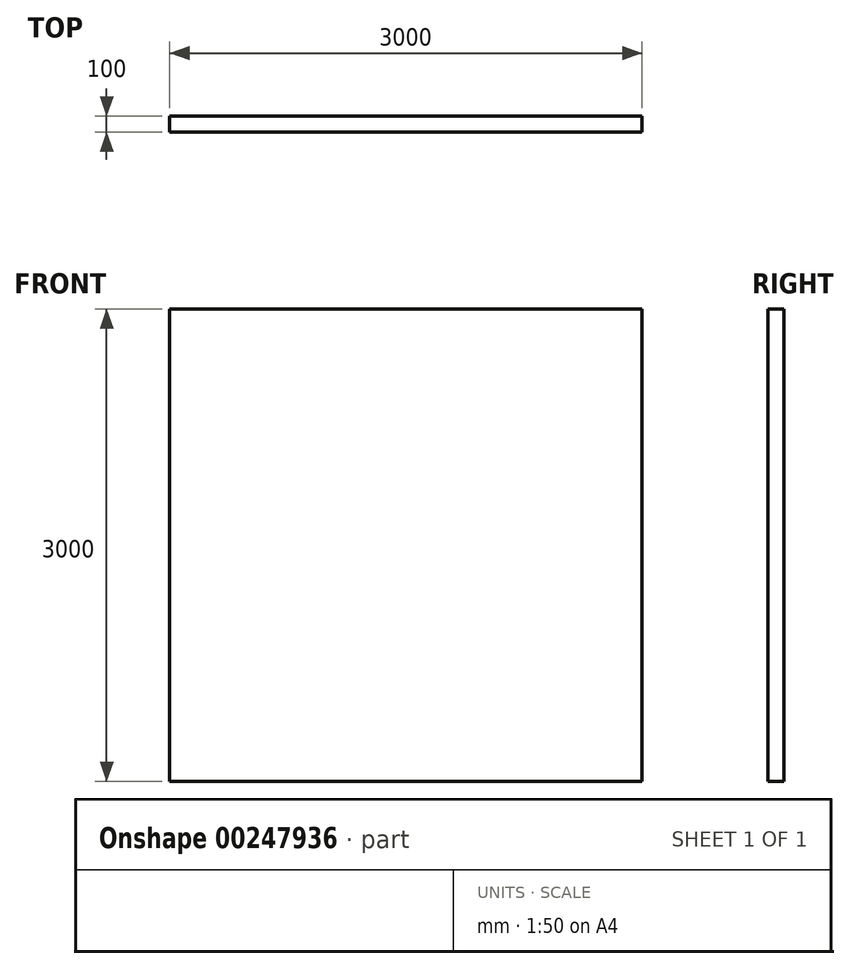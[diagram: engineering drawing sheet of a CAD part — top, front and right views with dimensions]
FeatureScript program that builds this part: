
annotation { "Feature Type Name" : "Feature", "Feature Type Description" : "" }
export const myFeature = defineFeature(function(context is Context, id is Id, definition is map)
    precondition{}
    {
        {
            var Q0;
            Q0=qCreatedBy(makeId("Front.planeOp"),FACE);
            var sketch = newSketch(context, id + "F0", { "sketchPlane" : qUnion([Q0])});
            skLineSegment(sketch, "E0.bottom", {"start": v(1500, 0) * mm, "end": v(-1500, 0) * mm});
            skLineSegment(sketch, "E0.top", {"start": v(1500, 3000) * mm, "end": v(-1500, 3000) * mm});
            skLineSegment(sketch, "E0.left", {"start": v(1500, 0) * mm, "end": v(1500, 3000) * mm});
            skLineSegment(sketch, "E0.right", {"start": v(-1500, 0) * mm, "end": v(-1500, 3000) * mm});
            skPoint(sketch, "E0.middle", {"position": v(0, 1500) * mm});
            skSolve(sketch);
        }
        {
            var Q0;
            Q0=makeQuery(id+"F0.imprint","IMPRINT",FACE,{"disambiguationData":[TD([[makeQuery(id+"F0.imprint","IMPRINT",EDGE,{"derivedFrom":sQuery(id+"F0.wireOp",EDGE,"E0.bottom")}),-1.0]])]});
            extrude(context, id + "F1", {"entities" : qUnion([Q0]), "endBound" : BoundingType.SYMMETRIC, "depth" : 100 * mm});
        }
    });
